# Revit family: Pump_Commercial-Effluent-Zoeller-270_Non_Automatic_Series
name_source: partatom
category: Mechanical Equipment
revit_build: Autodesk Revit 2014 (Build: 20130308_1515(x64)
units: mm (PartAtom-declared; Revit-internal decimal feet)

## types (2) — shared parameters
Apparent Load = 1725 VA
Assembly Code = D2010900
Cooling = Oil Filled
Cord Length = 240"
Cord Type = UL listed 3-wire neoprene cord and plug
Default Elevation = 0"
Description = Submersible sewage, *effluent or dewatering pumps.
Discharge Diameter = 2" NPT
Discharge Height = 6 3/16"
Discharge Radius = 1"
Height = 14 5/16"
Hertz = 60
Horse Power = 1
Impeller Type = Non-clogging vortex
Installation Type = Floor Mounted
Insulation = Class B
Length = 13 1/16"
Manufacturer = Zoeller
Material = Cast Iron-Zoeller-Powder Coated Epoxy
Max Flow Rate = 132 GPM
Max. Water Temp. = 54°C (130°F)
Maximum Head = 29'
Mechanical Seals = Carbon and Ceramic
Model = 270
Motor Thermal Shutoff = Auto Reset Thermal Overload (1 Ph).
Motor Type = Submersible
O-Rings and Cover Gasket = Neoprene
Operation = Non-Automatic
Phase = 1
Price = Prices may vary. Please consult Manufacturer Representative for most up-to-date price list.
Product Page URL = http://www.zoellerpumps.com
RPM = 3450
Revised Date = 2/22/2016
Shipping Weight = 49.00 lb
Solid Handling = 50 mm (2")
Type = Permanent Split Capacitor
Type Comments = Model 4270 features a cast iron base. BN and BE models include a variable level pump switch.
Additional cord lengths are available in 25' (8 m), 35' (11 m) and 50' (15 m).
URL = http://www.zoellerpumps.com
Warranty Information = 36 Months (Limited)
Waste Connection = Yes
Width = 9 1/2"

## per-type parameters (varying)
| type | Amps | Voltage |
| N270 | 15 A | 115 V |
| E270 | 8 A | 230 V |

## geometry (parser evidence)
native form markers: Sweep x3
no freeform markers — native parametric forms only
